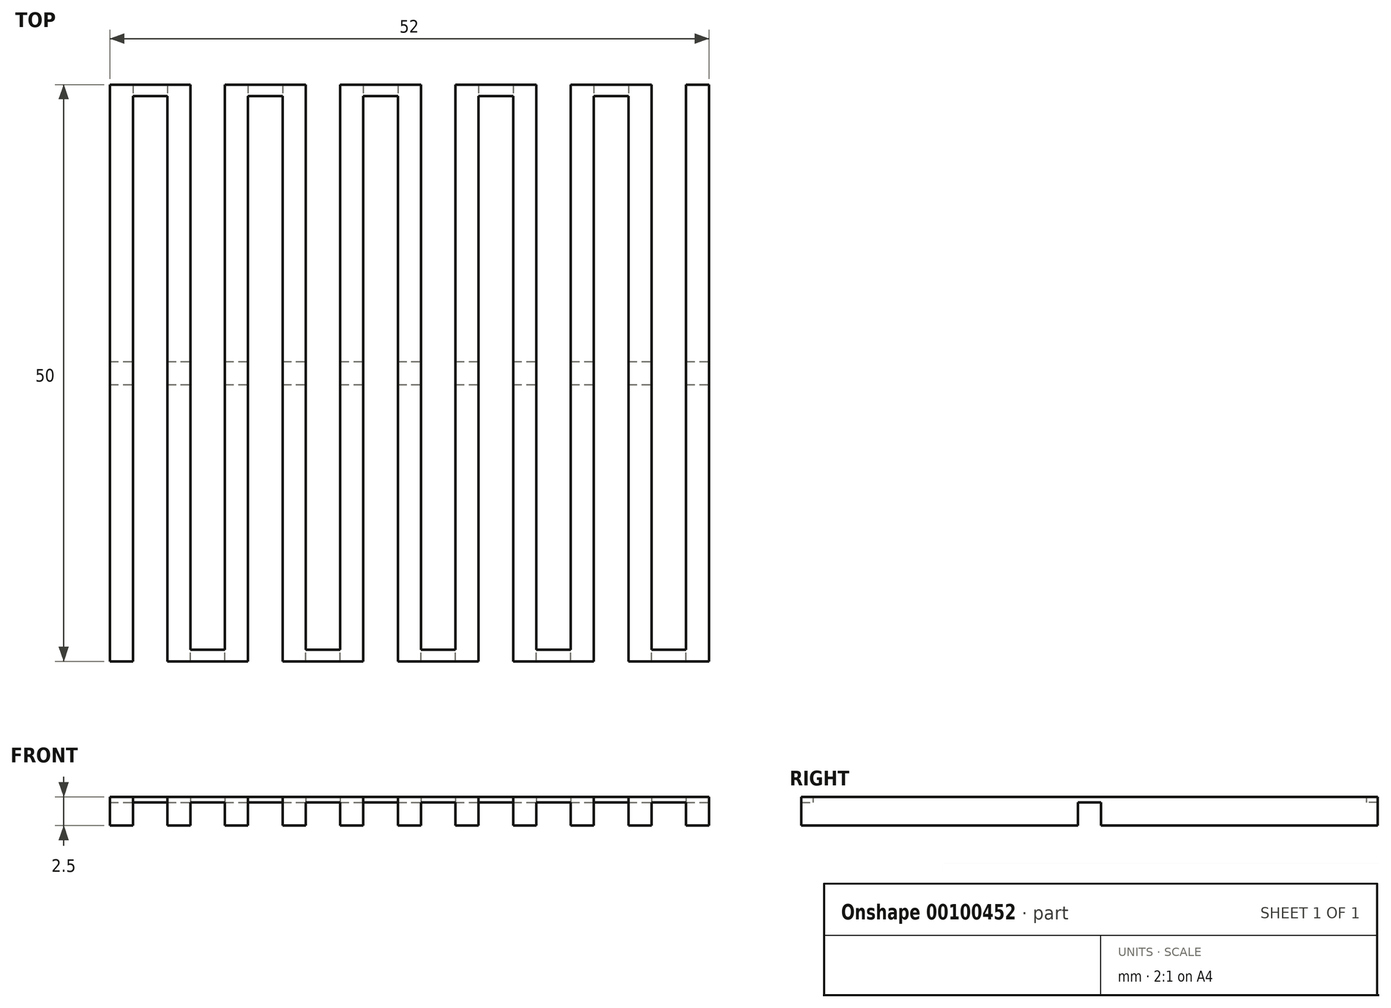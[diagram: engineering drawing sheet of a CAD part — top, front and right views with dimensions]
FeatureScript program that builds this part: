
annotation { "Feature Type Name" : "Feature", "Feature Type Description" : "" }
export const myFeature = defineFeature(function(context is Context, id is Id, definition is map)
    precondition{}
    {
        {
            var Q0;
            Q0=qCreatedBy(makeId("Top.planeOp"),FACE);
            var sketch = newSketch(context, id + "F0", { "sketchPlane" : qUnion([Q0])});
            skLineSegment(sketch, "E0", {"start": v(0, 0) * mm, "end": v(0, -50) * mm});
            skLineSegment(sketch, "E1", {"start": v(0, -50) * mm, "end": v(2, -50) * mm});
            skLineSegment(sketch, "E2", {"start": v(2, -50) * mm, "end": v(2, -1) * mm});
            skLineSegment(sketch, "E3", {"start": v(2, -1) * mm, "end": v(5, -1) * mm});
            skLineSegment(sketch, "E4", {"start": v(5, -1) * mm, "end": v(5, -50) * mm});
            skLineSegment(sketch, "E5", {"start": v(5, -50) * mm, "end": v(12, -50) * mm});
            skLineSegment(sketch, "E6", {"start": v(12, -50) * mm, "end": v(12, -1) * mm});
            skLineSegment(sketch, "E7", {"start": v(0, 0) * mm, "end": v(7, 0) * mm});
            skLineSegment(sketch, "E8", {"start": v(7, 0) * mm, "end": v(7, -49) * mm});
            skLineSegment(sketch, "E9", {"start": v(7, -49) * mm, "end": v(10, -49) * mm});
            skLineSegment(sketch, "E10", {"start": v(10, -49) * mm, "end": v(10, 0) * mm});
            skLineSegment(sketch, "E11", {"start": v(7, -24.5) * mm, "end": v(5, -24.5) * mm, "construction": true});
            skLineSegment(sketch, "E12", {"start": v(2, -25.5) * mm, "end": v(0, -25.5) * mm, "construction": true});
            skLineSegment(sketch, "E13", {"start": v(8.5, -49) * mm, "end": v(8.5, -50) * mm, "construction": true});
            skLineSegment(sketch, "E14", {"start": v(3.5, -1) * mm, "end": v(3.5, 0) * mm, "construction": true});
            skLineSegment(sketch, "E15.1.0.0", {"start": v(15, -50) * mm, "end": v(22, -50) * mm});
            skLineSegment(sketch, "E15.1.0.1", {"start": v(17, 0) * mm, "end": v(17, -49) * mm});
            skLineSegment(sketch, "E15.1.0.2", {"start": v(20, -49) * mm, "end": v(20, 0) * mm});
            skLineSegment(sketch, "E15.1.0.3", {"start": v(15, -1) * mm, "end": v(15, -50) * mm});
            skLineSegment(sketch, "E15.1.0.4", {"start": v(22, -50) * mm, "end": v(22, -1) * mm});
            skLineSegment(sketch, "E15.1.0.5", {"start": v(18.5, -49) * mm, "end": v(18.5, -50) * mm, "construction": true});
            skLineSegment(sketch, "E15.1.0.6", {"start": v(17, -24.5) * mm, "end": v(15, -24.5) * mm, "construction": true});
            skLineSegment(sketch, "E15.1.0.7", {"start": v(17, -49) * mm, "end": v(20, -49) * mm});
            skLineSegment(sketch, "E15.1.0.8", {"start": v(12, -1) * mm, "end": v(15, -1) * mm});
            skLineSegment(sketch, "E15.1.0.9", {"start": v(10, 0) * mm, "end": v(17, 0) * mm});
            skLineSegment(sketch, "E15.2.0.0", {"start": v(25, -50) * mm, "end": v(32, -50) * mm});
            skLineSegment(sketch, "E15.2.0.1", {"start": v(27, 0) * mm, "end": v(27, -49) * mm});
            skLineSegment(sketch, "E15.2.0.2", {"start": v(30, -49) * mm, "end": v(30, 0) * mm});
            skLineSegment(sketch, "E15.2.0.3", {"start": v(25, -1) * mm, "end": v(25, -50) * mm});
            skLineSegment(sketch, "E15.2.0.4", {"start": v(32, -50) * mm, "end": v(32, -1) * mm});
            skLineSegment(sketch, "E15.2.0.5", {"start": v(28.5, -49) * mm, "end": v(28.5, -50) * mm, "construction": true});
            skLineSegment(sketch, "E15.2.0.6", {"start": v(27, -24.5) * mm, "end": v(25, -24.5) * mm, "construction": true});
            skLineSegment(sketch, "E15.2.0.7", {"start": v(27, -49) * mm, "end": v(30, -49) * mm});
            skLineSegment(sketch, "E15.2.0.8", {"start": v(22, -1) * mm, "end": v(25, -1) * mm});
            skLineSegment(sketch, "E15.2.0.9", {"start": v(20, 0) * mm, "end": v(27, 0) * mm});
            skLineSegment(sketch, "E15.3.0.0", {"start": v(35, -50) * mm, "end": v(42, -50) * mm});
            skLineSegment(sketch, "E15.3.0.1", {"start": v(37, 0) * mm, "end": v(37, -49) * mm});
            skLineSegment(sketch, "E15.3.0.2", {"start": v(40, -49) * mm, "end": v(40, 0) * mm});
            skLineSegment(sketch, "E15.3.0.3", {"start": v(35, -1) * mm, "end": v(35, -50) * mm});
            skLineSegment(sketch, "E15.3.0.4", {"start": v(42, -50) * mm, "end": v(42, -1) * mm});
            skLineSegment(sketch, "E15.3.0.5", {"start": v(38.5, -49) * mm, "end": v(38.5, -50) * mm, "construction": true});
            skLineSegment(sketch, "E15.3.0.6", {"start": v(37, -24.5) * mm, "end": v(35, -24.5) * mm, "construction": true});
            skLineSegment(sketch, "E15.3.0.7", {"start": v(37, -49) * mm, "end": v(40, -49) * mm});
            skLineSegment(sketch, "E15.3.0.8", {"start": v(32, -1) * mm, "end": v(35, -1) * mm});
            skLineSegment(sketch, "E15.3.0.9", {"start": v(30, 0) * mm, "end": v(37, 0) * mm});
            skLineSegment(sketch, "E15.4.0.0", {"start": v(45, -50) * mm, "end": v(52, -50) * mm});
            skLineSegment(sketch, "E15.4.0.1", {"start": v(47, 0) * mm, "end": v(47, -49) * mm});
            skLineSegment(sketch, "E15.4.0.2", {"start": v(50, -49) * mm, "end": v(50, 0) * mm});
            skLineSegment(sketch, "E15.4.0.3", {"start": v(45, -1) * mm, "end": v(45, -50) * mm});
            skLineSegment(sketch, "E15.4.0.4", {"start": v(52, -50) * mm, "end": v(52, -1) * mm});
            skLineSegment(sketch, "E15.4.0.5", {"start": v(48.5, -49) * mm, "end": v(48.5, -50) * mm, "construction": true});
            skLineSegment(sketch, "E15.4.0.6", {"start": v(47, -24.5) * mm, "end": v(45, -24.5) * mm, "construction": true});
            skLineSegment(sketch, "E15.4.0.7", {"start": v(47, -49) * mm, "end": v(50, -49) * mm});
            skLineSegment(sketch, "E15.4.0.8", {"start": v(42, -1) * mm, "end": v(45, -1) * mm});
            skLineSegment(sketch, "E15.4.0.9", {"start": v(40, 0) * mm, "end": v(47, 0) * mm});
            skLineSegment(sketch, "E15.direction1", {"start": v(5, -50) * mm, "end": v(15, -50) * mm, "construction": true});
            skLineSegment(sketch, "E16", {"start": v(50, 0) * mm, "end": v(52, 0) * mm});
            skLineSegment(sketch, "E17", {"start": v(52, 0) * mm, "end": v(52, -1) * mm});
            skSolve(sketch);
        }
        {
            var Q0;
            Q0 = qSketchRegion(id + "F0", true);
            extrude(context, id + "F1", {"entities" : qUnion([Q0]), "depth" : .5 * mm});
        }
        {
            var Q0;
            Q0=makeQuery(id+"F1.opExtrude","CAP_FACE",FACE,{"disambiguationData":[OSD([sQuery(id+"F0.wireOp",EDGE,"E0"),sQuery(id+"F0.wireOp",EDGE,"E1"),sQuery(id+"F0.wireOp",EDGE,"E2"),sQuery(id+"F0.wireOp",EDGE,"E3"),sQuery(id+"F0.wireOp",EDGE,"3hrvP9vn-x9Tq-eIGn-EdKX-OppKwXInqQPx"),sQuery(id+"F0.wireOp",EDGE,"XfPTBOyJ-oBH1-B9e0-N9On-msEnOV8IjjkD"),sQuery(id+"F0.wireOp",EDGE,"qTP0CpO6-MGxY-lnJ0-z8Mm-3C7k6DRQJTo5"),sQuery(id+"F0.wireOp",EDGE,"VU3JISDy-RRCK-CBGG-0M1A-3kvs7zLeNf0a"),sQuery(id+"F0.wireOp",EDGE,"ef68386b-28ef-48a2-8401-d385efb9b2e6.1.0.0"),sQuery(id+"F0.wireOp",EDGE,"ef68386b-28ef-48a2-8401-d385efb9b2e6.1.0.1"),sQuery(id+"F0.wireOp",EDGE,"ef68386b-28ef-48a2-8401-d385efb9b2e6.1.0.2"),sQuery(id+"F0.wireOp",EDGE,"ef68386b-28ef-48a2-8401-d385efb9b2e6.1.0.3"),sQuery(id+"F0.wireOp",EDGE,"ef68386b-28ef-48a2-8401-d385efb9b2e6.2.0.0"),sQuery(id+"F0.wireOp",EDGE,"ef68386b-28ef-48a2-8401-d385efb9b2e6.2.0.1"),sQuery(id+"F0.wireOp",EDGE,"ef68386b-28ef-48a2-8401-d385efb9b2e6.2.0.2"),sQuery(id+"F0.wireOp",EDGE,"ef68386b-28ef-48a2-8401-d385efb9b2e6.2.0.3"),sQuery(id+"F0.wireOp",EDGE,"ef68386b-28ef-48a2-8401-d385efb9b2e6.3.0.0"),sQuery(id+"F0.wireOp",EDGE,"ef68386b-28ef-48a2-8401-d385efb9b2e6.3.0.1"),sQuery(id+"F0.wireOp",EDGE,"ef68386b-28ef-48a2-8401-d385efb9b2e6.3.0.2"),sQuery(id+"F0.wireOp",EDGE,"ef68386b-28ef-48a2-8401-d385efb9b2e6.3.0.3"),sQuery(id+"F0.wireOp",EDGE,"ef68386b-28ef-48a2-8401-d385efb9b2e6.4.0.0"),sQuery(id+"F0.wireOp",EDGE,"ef68386b-28ef-48a2-8401-d385efb9b2e6.4.0.1"),sQuery(id+"F0.wireOp",EDGE,"ef68386b-28ef-48a2-8401-d385efb9b2e6.4.0.2"),sQuery(id+"F0.wireOp",EDGE,"ef68386b-28ef-48a2-8401-d385efb9b2e6.4.0.3"),sQuery(id+"F0.wireOp",EDGE,"ef68386b-28ef-48a2-8401-d385efb9b2e6.5.0.0"),sQuery(id+"F0.wireOp",EDGE,"ef68386b-28ef-48a2-8401-d385efb9b2e6.5.0.1"),sQuery(id+"F0.wireOp",EDGE,"ef68386b-28ef-48a2-8401-d385efb9b2e6.5.0.2"),sQuery(id+"F0.wireOp",EDGE,"ef68386b-28ef-48a2-8401-d385efb9b2e6.5.0.3"),sQuery(id+"F0.wireOp",EDGE,"ef68386b-28ef-48a2-8401-d385efb9b2e6.6.0.0"),sQuery(id+"F0.wireOp",EDGE,"ef68386b-28ef-48a2-8401-d385efb9b2e6.6.0.1"),sQuery(id+"F0.wireOp",EDGE,"ef68386b-28ef-48a2-8401-d385efb9b2e6.6.0.2"),sQuery(id+"F0.wireOp",EDGE,"ef68386b-28ef-48a2-8401-d385efb9b2e6.6.0.3"),sQuery(id+"F0.wireOp",EDGE,"ef68386b-28ef-48a2-8401-d385efb9b2e6.7.0.0"),sQuery(id+"F0.wireOp",EDGE,"ef68386b-28ef-48a2-8401-d385efb9b2e6.7.0.1"),sQuery(id+"F0.wireOp",EDGE,"ef68386b-28ef-48a2-8401-d385efb9b2e6.7.0.2"),sQuery(id+"F0.wireOp",EDGE,"ef68386b-28ef-48a2-8401-d385efb9b2e6.7.0.3"),sQuery(id+"F0.wireOp",EDGE,"ef68386b-28ef-48a2-8401-d385efb9b2e6.8.0.0"),sQuery(id+"F0.wireOp",EDGE,"ef68386b-28ef-48a2-8401-d385efb9b2e6.8.0.3"),sQuery(id+"F0.wireOp",EDGE,"jQj3XcIf-TDLG-JvHT-7VaV-LChZkEZwnGAf"),sQuery(id+"F0.wireOp",EDGE,"CK0AClYK-FGTo-3Y4W-kOdt-9XT5PVUUsrSH")])],"isStart":true});
            var sketch = newSketch(context, id + "F2", { "sketchPlane" : qUnion([Q0])});
            skLineSegment(sketch, "E18.bottom", {"start": v(0, 0) * mm, "end": v(2, 0) * mm});
            skLineSegment(sketch, "E18.top", {"start": v(0, 24) * mm, "end": v(2, 24) * mm});
            skLineSegment(sketch, "E18.left", {"start": v(0, 0) * mm, "end": v(0, 24) * mm});
            skLineSegment(sketch, "E18.right", {"start": v(2, 0) * mm, "end": v(2, 24) * mm});
            skLineSegment(sketch, "E19.bottom", {"start": v(0, 50) * mm, "end": v(2, 50) * mm});
            skLineSegment(sketch, "E19.top", {"start": v(0, 26) * mm, "end": v(2, 26) * mm});
            skLineSegment(sketch, "E19.left", {"start": v(0, 50) * mm, "end": v(0, 26) * mm});
            skLineSegment(sketch, "E19.right", {"start": v(2, 50) * mm, "end": v(2, 26) * mm});
            skLineSegment(sketch, "E20.1.0.0", {"start": v(5, 0) * mm, "end": v(7, 0) * mm});
            skLineSegment(sketch, "E20.1.0.1", {"start": v(5, 24) * mm, "end": v(7, 24) * mm});
            skLineSegment(sketch, "E20.1.0.2", {"start": v(5, 0) * mm, "end": v(5, 24) * mm});
            skLineSegment(sketch, "E20.1.0.3", {"start": v(7, 0) * mm, "end": v(7, 24) * mm});
            skLineSegment(sketch, "E20.1.0.4", {"start": v(5, 50) * mm, "end": v(7, 50) * mm});
            skLineSegment(sketch, "E20.1.0.5", {"start": v(7, 50) * mm, "end": v(7, 26) * mm});
            skLineSegment(sketch, "E20.1.0.6", {"start": v(5, 50) * mm, "end": v(5, 26) * mm});
            skLineSegment(sketch, "E20.1.0.7", {"start": v(5, 26) * mm, "end": v(7, 26) * mm});
            skLineSegment(sketch, "E20.2.0.0", {"start": v(10, 0) * mm, "end": v(12, 0) * mm});
            skLineSegment(sketch, "E20.2.0.1", {"start": v(10, 24) * mm, "end": v(12, 24) * mm});
            skLineSegment(sketch, "E20.2.0.2", {"start": v(10, 0) * mm, "end": v(10, 24) * mm});
            skLineSegment(sketch, "E20.2.0.3", {"start": v(12, 0) * mm, "end": v(12, 24) * mm});
            skLineSegment(sketch, "E20.2.0.4", {"start": v(10, 50) * mm, "end": v(12, 50) * mm});
            skLineSegment(sketch, "E20.2.0.5", {"start": v(12, 50) * mm, "end": v(12, 26) * mm});
            skLineSegment(sketch, "E20.2.0.6", {"start": v(10, 50) * mm, "end": v(10, 26) * mm});
            skLineSegment(sketch, "E20.2.0.7", {"start": v(10, 26) * mm, "end": v(12, 26) * mm});
            skLineSegment(sketch, "E20.3.0.0", {"start": v(15, 0) * mm, "end": v(17, 0) * mm});
            skLineSegment(sketch, "E20.3.0.1", {"start": v(15, 24) * mm, "end": v(17, 24) * mm});
            skLineSegment(sketch, "E20.3.0.2", {"start": v(15, 0) * mm, "end": v(15, 24) * mm});
            skLineSegment(sketch, "E20.3.0.3", {"start": v(17, 0) * mm, "end": v(17, 24) * mm});
            skLineSegment(sketch, "E20.3.0.4", {"start": v(15, 50) * mm, "end": v(17, 50) * mm});
            skLineSegment(sketch, "E20.3.0.5", {"start": v(17, 50) * mm, "end": v(17, 26) * mm});
            skLineSegment(sketch, "E20.3.0.6", {"start": v(15, 50) * mm, "end": v(15, 26) * mm});
            skLineSegment(sketch, "E20.3.0.7", {"start": v(15, 26) * mm, "end": v(17, 26) * mm});
            skLineSegment(sketch, "E20.4.0.0", {"start": v(20, 0) * mm, "end": v(22, 0) * mm});
            skLineSegment(sketch, "E20.4.0.1", {"start": v(20, 24) * mm, "end": v(22, 24) * mm});
            skLineSegment(sketch, "E20.4.0.2", {"start": v(20, 0) * mm, "end": v(20, 24) * mm});
            skLineSegment(sketch, "E20.4.0.3", {"start": v(22, 0) * mm, "end": v(22, 24) * mm});
            skLineSegment(sketch, "E20.4.0.4", {"start": v(20, 50) * mm, "end": v(22, 50) * mm});
            skLineSegment(sketch, "E20.4.0.5", {"start": v(22, 50) * mm, "end": v(22, 26) * mm});
            skLineSegment(sketch, "E20.4.0.6", {"start": v(20, 50) * mm, "end": v(20, 26) * mm});
            skLineSegment(sketch, "E20.4.0.7", {"start": v(20, 26) * mm, "end": v(22, 26) * mm});
            skLineSegment(sketch, "E20.5.0.0", {"start": v(25, 0) * mm, "end": v(27, 0) * mm});
            skLineSegment(sketch, "E20.5.0.1", {"start": v(25, 24) * mm, "end": v(27, 24) * mm});
            skLineSegment(sketch, "E20.5.0.2", {"start": v(25, 0) * mm, "end": v(25, 24) * mm});
            skLineSegment(sketch, "E20.5.0.3", {"start": v(27, 0) * mm, "end": v(27, 24) * mm});
            skLineSegment(sketch, "E20.5.0.4", {"start": v(25, 50) * mm, "end": v(27, 50) * mm});
            skLineSegment(sketch, "E20.5.0.5", {"start": v(27, 50) * mm, "end": v(27, 26) * mm});
            skLineSegment(sketch, "E20.5.0.6", {"start": v(25, 50) * mm, "end": v(25, 26) * mm});
            skLineSegment(sketch, "E20.5.0.7", {"start": v(25, 26) * mm, "end": v(27, 26) * mm});
            skLineSegment(sketch, "E20.6.0.0", {"start": v(30, 0) * mm, "end": v(32, 0) * mm});
            skLineSegment(sketch, "E20.6.0.1", {"start": v(30, 24) * mm, "end": v(32, 24) * mm});
            skLineSegment(sketch, "E20.6.0.2", {"start": v(30, 0) * mm, "end": v(30, 24) * mm});
            skLineSegment(sketch, "E20.6.0.3", {"start": v(32, 0) * mm, "end": v(32, 24) * mm});
            skLineSegment(sketch, "E20.6.0.4", {"start": v(30, 50) * mm, "end": v(32, 50) * mm});
            skLineSegment(sketch, "E20.6.0.5", {"start": v(32, 50) * mm, "end": v(32, 26) * mm});
            skLineSegment(sketch, "E20.6.0.6", {"start": v(30, 50) * mm, "end": v(30, 26) * mm});
            skLineSegment(sketch, "E20.6.0.7", {"start": v(30, 26) * mm, "end": v(32, 26) * mm});
            skLineSegment(sketch, "E20.7.0.0", {"start": v(35, 0) * mm, "end": v(37, 0) * mm});
            skLineSegment(sketch, "E20.7.0.1", {"start": v(35, 24) * mm, "end": v(37, 24) * mm});
            skLineSegment(sketch, "E20.7.0.2", {"start": v(35, 0) * mm, "end": v(35, 24) * mm});
            skLineSegment(sketch, "E20.7.0.3", {"start": v(37, 0) * mm, "end": v(37, 24) * mm});
            skLineSegment(sketch, "E20.7.0.4", {"start": v(35, 50) * mm, "end": v(37, 50) * mm});
            skLineSegment(sketch, "E20.7.0.5", {"start": v(37, 50) * mm, "end": v(37, 26) * mm});
            skLineSegment(sketch, "E20.7.0.6", {"start": v(35, 50) * mm, "end": v(35, 26) * mm});
            skLineSegment(sketch, "E20.7.0.7", {"start": v(35, 26) * mm, "end": v(37, 26) * mm});
            skLineSegment(sketch, "E20.8.0.0", {"start": v(40, 0) * mm, "end": v(42, 0) * mm});
            skLineSegment(sketch, "E20.8.0.1", {"start": v(40, 24) * mm, "end": v(42, 24) * mm});
            skLineSegment(sketch, "E20.8.0.2", {"start": v(40, 0) * mm, "end": v(40, 24) * mm});
            skLineSegment(sketch, "E20.8.0.3", {"start": v(42, 0) * mm, "end": v(42, 24) * mm});
            skLineSegment(sketch, "E20.8.0.4", {"start": v(40, 50) * mm, "end": v(42, 50) * mm});
            skLineSegment(sketch, "E20.8.0.5", {"start": v(42, 50) * mm, "end": v(42, 26) * mm});
            skLineSegment(sketch, "E20.8.0.6", {"start": v(40, 50) * mm, "end": v(40, 26) * mm});
            skLineSegment(sketch, "E20.8.0.7", {"start": v(40, 26) * mm, "end": v(42, 26) * mm});
            skLineSegment(sketch, "E20.9.0.0", {"start": v(45, 0) * mm, "end": v(47, 0) * mm});
            skLineSegment(sketch, "E20.9.0.1", {"start": v(45, 24) * mm, "end": v(47, 24) * mm});
            skLineSegment(sketch, "E20.9.0.2", {"start": v(45, 0) * mm, "end": v(45, 24) * mm});
            skLineSegment(sketch, "E20.9.0.3", {"start": v(47, 0) * mm, "end": v(47, 24) * mm});
            skLineSegment(sketch, "E20.9.0.4", {"start": v(45, 50) * mm, "end": v(47, 50) * mm});
            skLineSegment(sketch, "E20.9.0.5", {"start": v(47, 50) * mm, "end": v(47, 26) * mm});
            skLineSegment(sketch, "E20.9.0.6", {"start": v(45, 50) * mm, "end": v(45, 26) * mm});
            skLineSegment(sketch, "E20.9.0.7", {"start": v(45, 26) * mm, "end": v(47, 26) * mm});
            skLineSegment(sketch, "E20.direction1", {"start": v(0, 0) * mm, "end": v(5, 0) * mm, "construction": true});
            skLineSegment(sketch, "E21.0.10.0", {"start": v(50, 0) * mm, "end": v(52, 0) * mm});
            skLineSegment(sketch, "E21.3.10.0", {"start": v(50, 24) * mm, "end": v(52, 24) * mm});
            skLineSegment(sketch, "E21.6.10.0", {"start": v(50, 0) * mm, "end": v(50, 24) * mm});
            skLineSegment(sketch, "E21.9.10.0", {"start": v(52, 0) * mm, "end": v(52, 24) * mm});
            skLineSegment(sketch, "E21.12.10.0", {"start": v(50, 50) * mm, "end": v(52, 50) * mm});
            skLineSegment(sketch, "E21.15.10.0", {"start": v(52, 50) * mm, "end": v(52, 26) * mm});
            skLineSegment(sketch, "E21.18.10.0", {"start": v(50, 50) * mm, "end": v(50, 26) * mm});
            skLineSegment(sketch, "E21.21.10.0", {"start": v(50, 26) * mm, "end": v(52, 26) * mm});
            skSolve(sketch);
        }
        {
            var Q0;
            Q0 = qSketchRegion(id + "F2", true);
            extrude(context, id + "F3", {"entities" : qUnion([Q0]), "operationType" : NewBodyOperationType.ADD, "depth" : 2 * mm});
        }
    });
